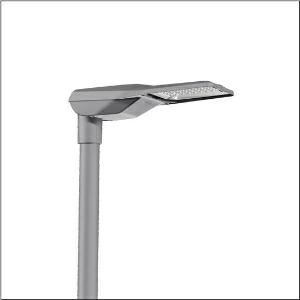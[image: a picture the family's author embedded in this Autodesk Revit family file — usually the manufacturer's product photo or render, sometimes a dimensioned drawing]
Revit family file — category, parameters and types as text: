
# Revit family: streetlight_sl_21_iq_mini___stw1_0a_5xe2e31d08gb_aef3
name_source: partatom
category: Lighting Fixtures
units: mm (PartAtom-declared; Revit-internal decimal feet)

## family parameters
Cut with Voids When Loaded = No
Host = Face
Light Source = No
Part Type = Normal
Room Calculation Point = No
Round Connector Dimension = Use Diameter
Shared = No

## types (1)
- --- (1 x LED, 5680 lm, 37.1 W, 3000K)
    Apparent Load = 37 VA
    CIE Flux Codes = 38 75 98 100 100
    Color Rendering = 70
    Color Temperature = 3000K
    Default Elevation = 1800 mm
    Description = Streetlight SL 21 iQ mini, mast luminaire, primary light control with lens, of PMMA, primary optical cover: cover, of toughened safety glass, transparent, light distribution: STW1.0a, light emission: direct distribution, primary light characteristic: asymmetric, installation type: post-top, side-entry, LED, High Power LED, rated luminous flux: 5.680lm, luminous efficacy: 153lm/W, light colour: 730, colour temperature: 3000K, control: Auto-Match, Temp-Guard, Lumen-Switch, Night-Set, Smart-Wire, Light-Fading, Desk-Remote (wireless, voltage-free reading and setting of iQ features in the workshop via application-optimized NFC function/RFID function), optimised constant luminous flux control (CLO 2.0), presetting dimming linear, mains connection: 220..240V, AC, 50/60Hz, start of lifetime: 37W, end of service life: 39W, reduction: 18W, luminaire housing, of diecast aluminium, powder-coated, Siteco® metallic grey (DB 702S), corrosivity category C5 mid according to DIN EN ISO 12944, please order mast flange separately, inclination adjustable: 0°, 5°, 10°, 15°, sealing non-destructively replaceable, multi-level sealing system, length: 628mm, width: 235mm, height: 110mm, mast flange for spigot size: 42mm (side-entry): 5XC10008XM4, 60/48mm (side-entry/post-top): 5XC10108XM2, 76/60mm (side-entry/post-top): 5XC10108XM1, protection rating (complete): IP66, insulation class (complete): insulation class II (safety insulation), certification: CE, ENEC, ENEC+, VDE, impact resistance: IK09, permissible operating ambient temperature for outdoor applications: -40..+50°C, standard-compliant lighting for roads and squares, packaging unit: 1 piece

Light Distribution: STW1.0a
    Height = 110 mm
    Lamp = 1 x LED
    Lamp Light Flux = 5680 lm
    Lamp Power = 37.1 W
    Lamp count = 1
    Length = 625 mm
    Luminous efficacy = 153 lm/W
    Manufacturer = Siteco
    ModVariant = No
    Model = 5XE2E31D08GB
    Number of Poles = 1
    OnlyDefault = Yes
    Power Factor = 1
    Product Name = Streetlight SL 21 iQ mini | STW1.0a
    Product group = mast luminaire | pylon top
    ProductGroupID = 6100
    Protection Class = Protection class II
    Protection Degree = IP 66
    RLX_Detail_Level = 1
    RLX_Emergency_Light_Flux = 0 lm
    RLX_Emergency_Type = 0
    RLX_Emergency_Type_DB = No
    RlxData = <blob elided: 92229 chars, md5=98d8028f>
    Socket = socket
    Standby Power = 0 W
    System Light Flux = 5680 lm
    System Power = 37 W
    Type Comments = factory setting: luminous flux: 100 % | dim-lin: 254 | 385 mA
    Type Image = l_1003519.jpg
    URL = http://relux.com
    VarID = @adj_139427
    Voltage = 0 V
    Weight = 0.00 kg
    Width = 234 mm

## geometry (parser evidence)
native form markers: Blend x4, Sweep x11
no freeform markers — native parametric forms only
